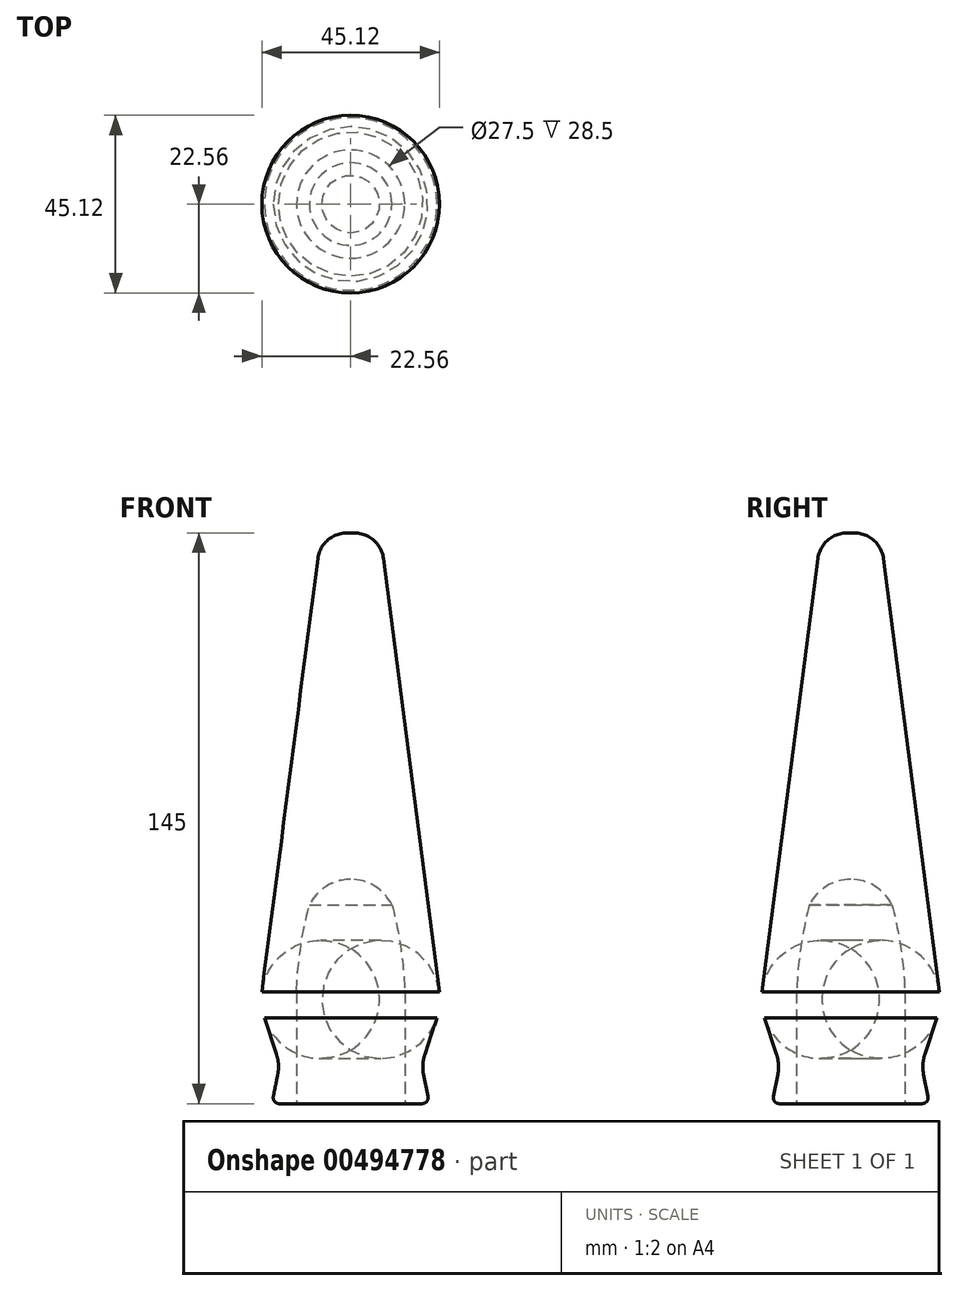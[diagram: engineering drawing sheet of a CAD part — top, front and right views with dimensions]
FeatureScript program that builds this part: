
annotation { "Feature Type Name" : "Feature", "Feature Type Description" : "" }
export const myFeature = defineFeature(function(context is Context, id is Id, definition is map)
    precondition{}
    {
        {
            var Q0;
            Q0=qCreatedBy(makeId("Front.planeOp"),FACE);
            var sketch = newSketch(context, id + "F0", { "sketchPlane" : qUnion([Q0])});
            skLineSegment(sketch, "E0", {"start": v(23, 0) * mm, "end": v(7.5, 120) * mm});
            skLineSegment(sketch, "E1", {"start": v(0, 120) * mm, "end": v(0, 32) * mm});
            skLineSegment(sketch, "E2", {"start": v(0, -27) * mm, "end": v(0, -53.61) * mm});
            skLineSegment(sketch, "E3", {"start": v(0, 120) * mm, "end": v(7.5, 120) * mm});
            skLineSegment(sketch, "E4", {"start": v(0, 123.57) * mm, "end": v(0, 137.09) * mm});
            skLineSegment(sketch, "E5", {"start": v(13.75, -25) * mm, "end": v(20, -25) * mm});
            skLineSegment(sketch, "E6", {"start": v(18, -15) * mm, "end": v(20, -25) * mm});
            skLineSegment(sketch, "E7", {"start": v(23, 0) * mm, "end": v(18, -15) * mm});
            skLineSegment(sketch, "E8", {"start": v(13.75, -25) * mm, "end": v(13.75, 1.5) * mm});
            skLineSegment(sketch, "E9", {"start": v(0, 32) * mm, "end": v(0, 32) * mm});
            skArc(sketch, "E10", {"start": v(10.5, 25.5) * mm, "mid": v(6.17, 30.24) * mm, "end": v(0, 32) * mm});
            skLineSegment(sketch, "E11", {"start": v(13.75, 1.5) * mm, "end": v(13.75, 3.5) * mm});
            skArc(sketch, "E12", {"start": v(13.8, 2.34) * mm, "mid": v(12.79, 14) * mm, "end": v(10.5, 25.5) * mm});
            skPoint(sketch, "E13.orphan", {"position": v(13.75, 32) * mm});
            skSolve(sketch);
        }
        {
            var Q0;
            Q0=makeQuery(id+"F0.imprint","IMPRINT",FACE,{"disambiguationData":[TD([[makeQuery(id+"F0.imprint","IMPRINT",EDGE,{"derivedFrom":sQuery(id+"F0.wireOp",EDGE,"E0")}),1.0]])]});
            var Q1;
            Q1=sQuery(id+"F0.wireOp",EDGE,"E4");
            revolve(context, id + "F1", {"entities" : qUnion([Q0]), "axis" : qUnion([Q1]), "revolveType" : RevolveType.ONE_DIRECTION, "angle" : 180 * degree});
        }
        {
            var Q0;
            Q0=makeQuery(id+"F1.opRevolve","SWEPT_BODY",BODY,{"disambiguationData":[OSD([sQuery(id+"F0.wireOp",EDGE,"E0"),sQuery(id+"F0.wireOp",EDGE,"E1"),sQuery(id+"F0.wireOp",EDGE,"E3"),sQuery(id+"F0.wireOp",EDGE,"E5"),sQuery(id+"F0.wireOp",EDGE,"E6"),sQuery(id+"F0.wireOp",EDGE,"7rPBSgOz-U2yj-cz9y-w9HN-AUau6IC02yR6"),sQuery(id+"F0.wireOp",EDGE,"7t8U0qsF-pLgd-GgIO-Hkkh-cJwSIB7hQWLG")])]});
            var Q1;
            Q1=qCreatedBy(makeId("Front.planeOp"),FACE);
            mirror(context, id + "F2", {"operationType" : NewBodyOperationType.ADD, "entities" : qUnion([Q0]), "mirrorPlane" : qUnion([Q1])});
        }
        {
            var Q0;
            {var subQ0=makeQuery(id+"F1.opRevolve","SWEPT_EDGE",EDGE,{"disambiguationData":[OSD([sQuery(id+"F0.wireOp",EDGE,"E0"),sQuery(id+"F0.wireOp",EDGE,"E3")])]});Q0=makeQuery(id+"F2.boolean.opBoolean","MERGE",EDGE,{"derivedFrom":[subQ0,makeQuery(id+"F2.opPattern","COPY",EDGE,{"derivedFrom":subQ0,"instanceName":"1"})]});}
            fillet(context, id + "F3", {"entities" : qUnion([Q0]), "radius" : 7.5 * mm, "tangentPropagation" : true, "allowEdgeOverflow" : false});
        }
        {
            var Q0;
            {var subQ0=makeQuery(id+"F1.opRevolve","SWEPT_EDGE",EDGE,{"disambiguationData":[OSD([sQuery(id+"F0.wireOp",EDGE,"E0"),sQuery(id+"F0.wireOp",EDGE,"E7")])]});Q0=makeQuery(id+"F2.boolean.opBoolean","MERGE",EDGE,{"derivedFrom":[subQ0,makeQuery(id+"F2.opPattern","COPY",EDGE,{"derivedFrom":subQ0,"instanceName":"1"})]});}
            fillet(context, id + "F4", {"entities" : qUnion([Q0]), "radius" : 15 * mm, "tangentPropagation" : true, "allowEdgeOverflow" : false});
        }
        {
            var Q0;
            {var subQ0=makeQuery(id+"F1.opRevolve","SWEPT_EDGE",EDGE,{"disambiguationData":[OSD([sQuery(id+"F0.wireOp",EDGE,"E5"),sQuery(id+"F0.wireOp",EDGE,"E6")])]});Q0=makeQuery(id+"F2.boolean.opBoolean","MERGE",EDGE,{"derivedFrom":[subQ0,makeQuery(id+"F2.opPattern","COPY",EDGE,{"derivedFrom":subQ0,"instanceName":"1"})]});}
            fillet(context, id + "F5", {"entities" : qUnion([Q0]), "radius" : 1.5 * mm, "tangentPropagation" : true, "allowEdgeOverflow" : false});
        }
        {
            var Q0;
            {var subQ0=makeQuery(id+"F1.opRevolve","SWEPT_EDGE",EDGE,{"disambiguationData":[OSD([sQuery(id+"F0.wireOp",EDGE,"E6"),sQuery(id+"F0.wireOp",EDGE,"E7")])]});Q0=makeQuery(id+"F2.boolean.opBoolean","MERGE",EDGE,{"derivedFrom":[subQ0,makeQuery(id+"F2.opPattern","COPY",EDGE,{"derivedFrom":subQ0,"instanceName":"1"})]});}
            fillet(context, id + "F6", {"entities" : qUnion([Q0]), "radius" : 10 * mm, "tangentPropagation" : true, "allowEdgeOverflow" : false});
        }
    });
